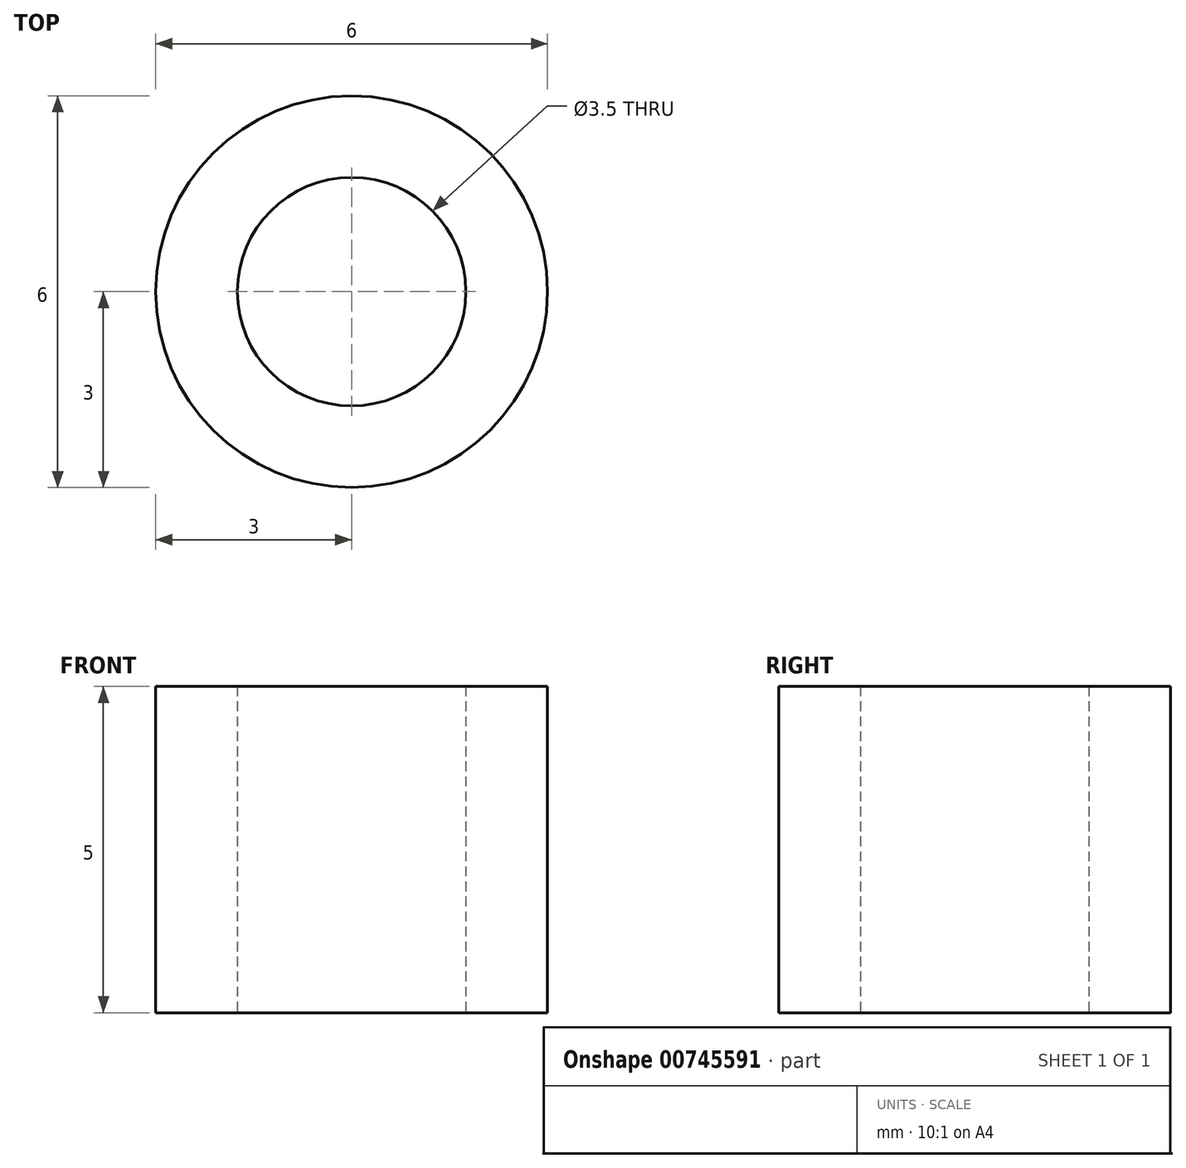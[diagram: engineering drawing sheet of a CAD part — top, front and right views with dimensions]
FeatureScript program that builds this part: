
annotation { "Feature Type Name" : "Feature", "Feature Type Description" : "" }
export const myFeature = defineFeature(function(context is Context, id is Id, definition is map)
    precondition{}
    {
        {
            var Q0;
            Q0=qCreatedBy(makeId("Top.planeOp"),FACE);
            var sketch = newSketch(context, id + "F0", { "sketchPlane" : qUnion([Q0])});
            skCircle(sketch, "E0", {"center": v(0, 0) * mm, "radius": 3 * mm});
            skCircle(sketch, "E1", {"center": v(0, 0) * mm, "radius": 1.75 * mm});
            skSolve(sketch);
        }
        {
            var Q0;
            Q0=makeQuery(id+"F0.imprint","IMPRINT",FACE,{"disambiguationData":[TD([[makeQuery(id+"F0.imprint","IMPRINT",EDGE,{"derivedFrom":sQuery(id+"F0.wireOp",EDGE,"E0")}),1.0]])]});
            extrude(context, id + "F1", {"entities" : qUnion([Q0]), "depth" : 5 * mm, "offsetDistance" : 25 * mm});
        }
    });
